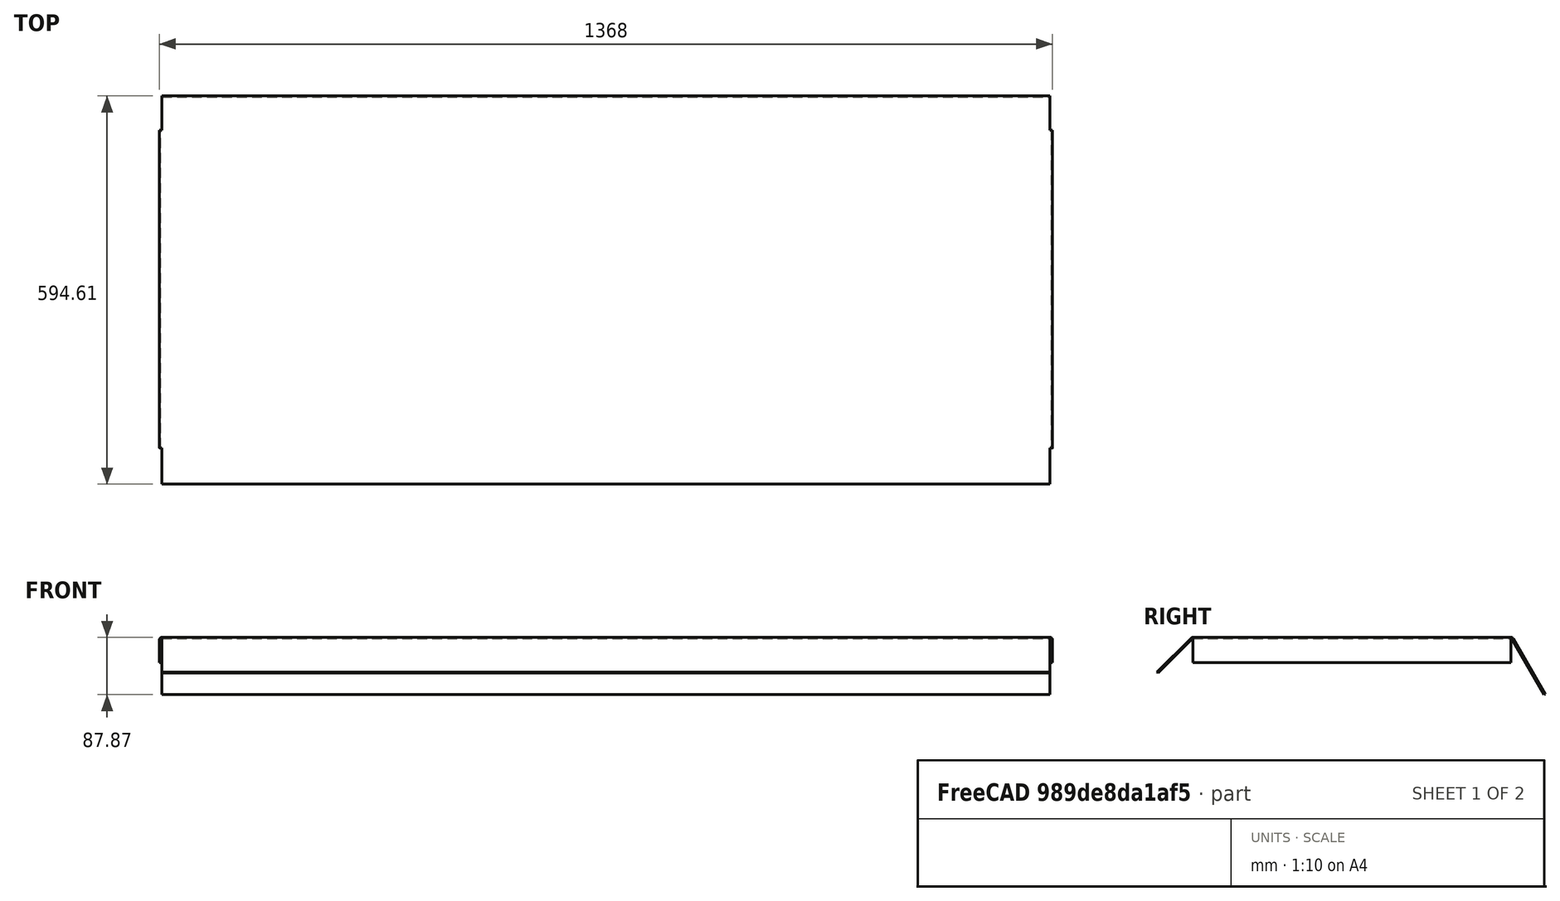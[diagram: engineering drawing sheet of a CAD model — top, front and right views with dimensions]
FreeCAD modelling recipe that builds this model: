
FCSTD DOCUMENT  (FreeCAD 0.20R29410 (Git))
Label: DeckblechV1test
License: All rights reserved
LicenseURL: http://en.wikipedia.org/wiki/All_rights_reserved
objects: PartDesign::FeaturePython×4, PartDesign::AdditiveBox×1, PartDesign::Body×1, Part::Feature×1, Sketcher::SketchObject×1
note: 9 computed .brp shape members not serialized (recipe doc carries the construction recipe); baked Part::Feature solids carry a one-line shape summary decoded from their .brp

FEATURE [PartDesign::AdditiveBox] Box
  AttacherType = Attacher::AttachEngine3D
  Height = 2
  Length = 1360
  MapMode = 5
  Refine = true
  Support = -> [XY_Plane]
  Width = 487
FEATURE [PartDesign::FeaturePython] Bend  # WARN: FeaturePython — macro-defined, semantics opaque (R4)
  AutoMiter = true
  BaseFeature = -> Box
  BendType = 0
  LengthList = [74]
  LengthSpec = 0
  ReliefFactor = 0.7
  UseReliefFactor = false
  angle = 45
  baseObject = -> Box [Edge9]
  bendAList = [45]
  extend1 = 0
  extend2 = 0
  gap1 = 0
  gap2 = 0
  invert = true
  kfactor = 0.5
  length = 74
  maxExtendDist = 5
  minGap = 0.1
  minReliefGap = 1
  miterangle1 = 0
  miterangle2 = 0
  offset = 0
  radius = 2
  reliefType = 0
  reliefd = 1
  reliefw = 0.8
  sketchflip = false
  sketchinvert = false
  unfold = false
FEATURE [PartDesign::FeaturePython] Bend001  # WARN: FeaturePython — macro-defined, semantics opaque (R4)
  AutoMiter = true
  BaseFeature = -> Bend
  BendType = 0
  LengthList = [98]
  LengthSpec = 0
  ReliefFactor = 0.7
  UseReliefFactor = false
  angle = 60
  baseObject = -> Bend [Edge24]
  bendAList = [60]
  extend1 = 0
  extend2 = 0
  gap1 = 0
  gap2 = 0
  invert = true
  kfactor = 0.5
  length = 98
  maxExtendDist = 5
  minGap = 0.1
  minReliefGap = 1
  miterangle1 = 0
  miterangle2 = 0
  offset = 0
  radius = 2
  reliefType = 0
  reliefd = 1
  reliefw = 0.8
  sketchflip = false
  sketchinvert = false
  unfold = false
FEATURE [PartDesign::FeaturePython] Bend002  # WARN: FeaturePython — macro-defined, semantics opaque (R4)
  AutoMiter = true
  BaseFeature = -> Bend001
  BendType = 0
  LengthList = [35]
  LengthSpec = 0
  ReliefFactor = 0.7
  UseReliefFactor = false
  angle = 90
  baseObject = -> Bend001 [Edge24]
  bendAList = [90]
  extend1 = 0
  extend2 = 0
  gap1 = 0
  gap2 = 0
  invert = true
  kfactor = 0.5
  length = 35
  maxExtendDist = 5
  minGap = 0.1
  minReliefGap = 1
  miterangle1 = 0
  miterangle2 = 0
  offset = 0
  radius = 2
  reliefType = 0
  reliefd = 1
  reliefw = 0.8
  sketchflip = false
  sketchinvert = false
  unfold = false
FEATURE [PartDesign::FeaturePython] Bend003  # WARN: FeaturePython — macro-defined, semantics opaque (R4)
  AutoMiter = true
  BaseFeature = -> Bend002
  BendType = 0
  LengthList = [35]
  LengthSpec = 0
  ReliefFactor = 0.7
  UseReliefFactor = false
  angle = 90
  baseObject = -> Bend002 [Edge24]
  bendAList = [90]
  extend1 = 0
  extend2 = 0
  gap1 = 0
  gap2 = 0
  invert = true
  kfactor = 0.5
  length = 35
  maxExtendDist = 5
  minGap = 0.1
  minReliefGap = 1
  miterangle1 = 0
  miterangle2 = 0
  offset = 0
  radius = 2
  reliefType = 0
  reliefd = 1
  reliefw = 0.8
  sketchflip = false
  sketchinvert = false
  unfold = false
FEATURE [PartDesign::Body] Body
  Group = -> [Box,Bend,Bend001,Bend002,Bend003]
  Origin = -> Origin
  Tip = -> Bend003
FEATURE [Part::Feature] Unfold
  shape: bbox 1438 x 566.3 x 2 mm, 12 faces (baked)
FEATURE [Sketcher::SketchObject] Unfold_Sketch
  FullyConstrained = false
  sketch-geometry (16):
    g0: LineSegment StartX=-38.7699 StartY=0 StartZ=0 EndX=-38.7699 EndY=487 EndZ=0
    g1: LineSegment StartX=1398.77 StartY=0 StartZ=0 EndX=1398.77 EndY=487 EndZ=0
    g2: LineSegment StartX=0 StartY=-75.885 StartZ=0 EndX=1360 EndY=-75.885 EndZ=0
    g3: LineSegment StartX=0 StartY=0 StartZ=0 EndX=0 EndY=-75.885 EndZ=0
    g4: LineSegment StartX=1360 StartY=-75.885 StartZ=0 EndX=1360 EndY=0 EndZ=0
    g5: LineSegment StartX=1360 StartY=0 StartZ=0 EndX=1398.77 EndY=0 EndZ=0
    g6: LineSegment StartX=1398.77 StartY=487 StartZ=0 EndX=1360 EndY=487 EndZ=0
    g7: LineSegment StartX=0 StartY=487 StartZ=0 EndX=1360 EndY=487 EndZ=0
    g8: LineSegment StartX=-38.7699 StartY=487 StartZ=0 EndX=0 EndY=487 EndZ=0
    g9: LineSegment StartX=0 StartY=0 StartZ=0 EndX=-38.7699 EndY=0 EndZ=0
    g10: BSplineCurve PolesCount=15 KnotsCount=15 Degree=1 IsPeriodic=0
    g11: BSplineCurve PolesCount=15 KnotsCount=15 Degree=1 IsPeriodic=0
    g12: LineSegment StartX=0 StartY=490.464 StartZ=0 EndX=1360 EndY=490.464 EndZ=0
    g13: LineSegment StartX=-1.88496 StartY=0 StartZ=0 EndX=-1.88496 EndY=487 EndZ=0
    g14: LineSegment StartX=1361.88 StartY=0 StartZ=0 EndX=1361.88 EndY=487 EndZ=0
    g15: LineSegment StartX=0 StartY=-0.942478 StartZ=0 EndX=1360 EndY=-0.942478 EndZ=0
